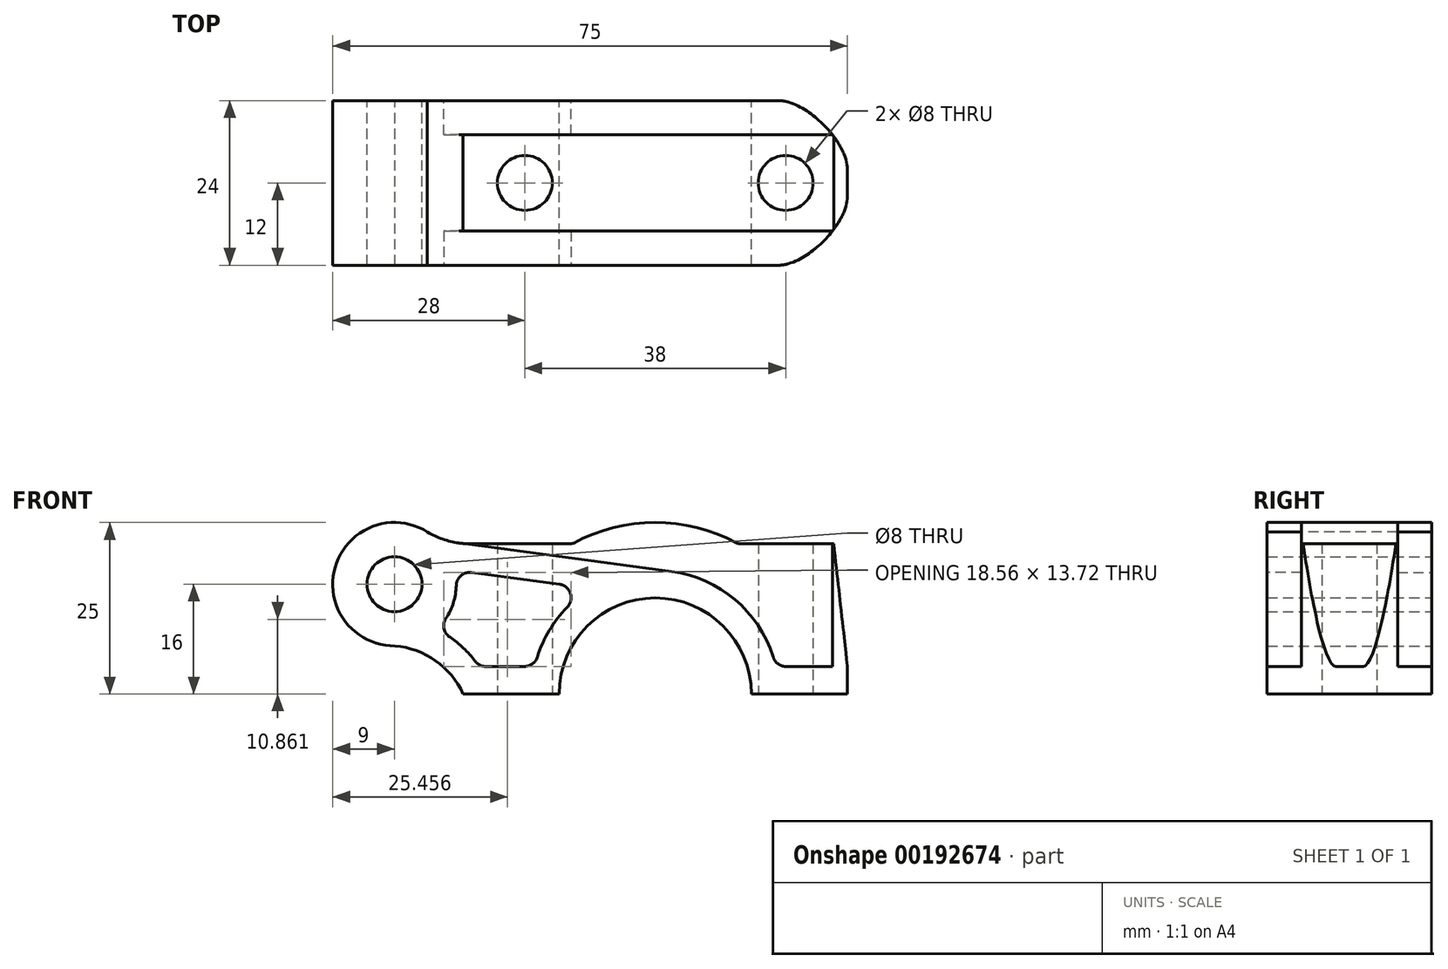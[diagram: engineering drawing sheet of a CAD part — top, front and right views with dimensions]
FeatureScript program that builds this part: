
annotation { "Feature Type Name" : "Feature", "Feature Type Description" : "" }
export const myFeature = defineFeature(function(context is Context, id is Id, definition is map)
    precondition{}
    {
        {
            var Q0;
            Q0=qCreatedBy(makeId("Front.planeOp"),FACE);
            var sketch = newSketch(context, id + "F0", { "sketchPlane" : qUnion([Q0])});
            skLineSegment(sketch, "E0.bottom", {"start": v(-28, 0) * mm, "end": v(-14, 0) * mm});
            skLineSegment(sketch, "E0.top", {"start": v(-28, 25) * mm, "end": v(28, 25) * mm});
            skLineSegment(sketch, "E0.left", {"start": v(-28, 0) * mm, "end": v(-28, 25) * mm});
            skLineSegment(sketch, "E0.right", {"start": v(28, 0) * mm, "end": v(28, 25) * mm});
            skArc(sketch, "E1", {"start": v(14, 0) * mm, "mid": v(0, 14) * mm, "end": v(-14, 0) * mm});
            skLineSegment(sketch, "E2.trimOffspring", {"start": v(14, 0) * mm, "end": v(28, 0) * mm});
            skSolve(sketch);
        }
        {
            var Q0;
            Q0 = qSketchRegion(id + "F0", true);
            extrude(context, id + "F1", {"entities" : qUnion([Q0]), "depth" : 24 * mm});
        }
        {
            var Q0;
            Q0=qCreatedBy(makeId("Top.planeOp"),FACE);
            var sketch = newSketch(context, id + "F2", { "sketchPlane" : qUnion([Q0])});
            skLineSegment(sketch, "E3", {"start": v(-28, -12) * mm, "end": v(28, -12) * mm, "construction": true});
            skCircle(sketch, "E4", {"center": v(-19, -12) * mm, "radius": 4 * mm});
            skCircle(sketch, "E5", {"center": v(19, -12) * mm, "radius": 4 * mm});
            skSolve(sketch);
        }
        {
            var Q0;
            Q0 = qSketchRegion(id + "F2", true);
            extrude(context, id + "F3", {"entities" : qUnion([Q0]), "operationType" : NewBodyOperationType.REMOVE, "endBound" : BoundingType.THROUGH_ALL, "depth" : 25 * mm});
        }
        {
            var Q0;
            Q0=qCreatedBy(makeId("Front.planeOp"),FACE);
            var sketch = newSketch(context, id + "F4", { "sketchPlane" : qUnion([Q0])});
            skCircle(sketch, "E6", {"center": v(-38, 16) * mm, "radius": 4 * mm});
            skArc(sketch, "E7", {"start": v(-38, 25) * mm, "mid": v(-47, 15.96) * mm, "end": v(-37.93, 7) * mm});
            skLineSegment(sketch, "E8", {"start": v(-38, 25) * mm, "end": v(-28, 25) * mm});
            skLineSegment(sketch, "E9", {"start": v(-28, 25) * mm, "end": v(-28, 0) * mm});
            skArc(sketch, "E10", {"start": v(-28, 0) * mm, "mid": v(-32.01, 4.85) * mm, "end": v(-37.93, 7) * mm});
            skSolve(sketch);
        }
        {
            var Q0;
            Q0 = qSketchRegion(id + "F4", true);
            extrude(context, id + "F5", {"entities" : qUnion([Q0]), "operationType" : NewBodyOperationType.ADD, "depth" : 24 * mm});
        }
        {
            var Q0;
            Q0=makeQuery(id+"F5.boolean.opBoolean","MERGE",FACE,{"derivedFrom":[makeQuery(id+"F1.opExtrude","CAP_FACE",FACE,{"disambiguationData":[OSD([sQuery(id+"F0.wireOp",EDGE,"E0.bottom"),sQuery(id+"F0.wireOp",EDGE,"E0.top"),sQuery(id+"F0.wireOp",EDGE,"E0.left"),sQuery(id+"F0.wireOp",EDGE,"E0.right"),sQuery(id+"F0.wireOp",EDGE,"E1"),sQuery(id+"F0.wireOp",EDGE,"E2.trimOffspring")])],"isStart":false}),makeQuery(id+"F5.opExtrude","CAP_FACE",FACE,{"disambiguationData":[OSD([sQuery(id+"F4.wireOp",EDGE,"E6"),sQuery(id+"F4.wireOp",EDGE,"E7"),sQuery(id+"F4.wireOp",EDGE,"E8"),sQuery(id+"F4.wireOp",EDGE,"E9"),sQuery(id+"F4.wireOp",EDGE,"E10")])],"isStart":false})]});
            var sketch = newSketch(context, id + "F6", { "sketchPlane" : qUnion([Q0])});
            skArc(sketch, "E11", {"start": v(12, 21.93) * mm, "mid": v(0, 25) * mm, "end": v(-12, 21.93) * mm});
            skLineSegment(sketch, "E12.bottom", {"start": v(12, 21.93) * mm, "end": v(28, 21.93) * mm});
            skLineSegment(sketch, "E12.top", {"start": v(12, 25) * mm, "end": v(28, 25) * mm});
            skLineSegment(sketch, "E12.right", {"start": v(28, 21.93) * mm, "end": v(28, 25) * mm});
            skLineSegment(sketch, "E13.MirrorCS", {"start": v(-12, 25) * mm, "end": v(-28, 25) * mm});
            skLineSegment(sketch, "E14.MirrorCS", {"start": v(-12, 21.93) * mm, "end": v(-28, 21.93) * mm});
            skLineSegment(sketch, "E15", {"start": v(12, 25) * mm, "end": v(-12, 25) * mm});
            skPoint(sketch, "E16.MirrorCS.start.orphan", {"position": v(-12, 21.93) * mm});
            skArc(sketch, "E17", {"start": v(-33.2, 23.61) * mm, "mid": v(-35.5, 24.65) * mm, "end": v(-38, 25) * mm});
            skLineSegment(sketch, "E18", {"start": v(-28, 25) * mm, "end": v(-38, 25) * mm});
            skPoint(sketch, "E19.MirrorCS.end.orphan", {"position": v(-28, 25) * mm});
            skPoint(sketch, "E20.start.orphan", {"position": v(-28, 21.93) * mm});
            skArc(sketch, "E21", {"start": v(-33.2, 23.61) * mm, "mid": v(-30.7, 22.47) * mm, "end": v(-28, 21.93) * mm});
            skSolve(sketch);
        }
        {
            var Q0;
            Q0 = qSketchRegion(id + "F6", true);
            extrude(context, id + "F7", {"entities" : qUnion([Q0]), "operationType" : NewBodyOperationType.REMOVE, "endBound" : BoundingType.THROUGH_ALL, "oppositeDirection" : true, "depth" : 25 * mm});
        }
        {
            var Q0;
            Q0=makeQuery(id+"F5.boolean.opBoolean","MERGE",FACE,{"derivedFrom":[makeQuery(id+"F1.opExtrude","CAP_FACE",FACE,{"disambiguationData":[OSD([sQuery(id+"F0.wireOp",EDGE,"E0.bottom"),sQuery(id+"F0.wireOp",EDGE,"E0.top"),sQuery(id+"F0.wireOp",EDGE,"E0.left"),sQuery(id+"F0.wireOp",EDGE,"E0.right"),sQuery(id+"F0.wireOp",EDGE,"E1"),sQuery(id+"F0.wireOp",EDGE,"E2.trimOffspring")])],"isStart":false}),makeQuery(id+"F5.opExtrude","CAP_FACE",FACE,{"disambiguationData":[OSD([sQuery(id+"F4.wireOp",EDGE,"E6"),sQuery(id+"F4.wireOp",EDGE,"E7"),sQuery(id+"F4.wireOp",EDGE,"E8"),sQuery(id+"F4.wireOp",EDGE,"E9"),sQuery(id+"F4.wireOp",EDGE,"E10")])],"isStart":false})]});
            var sketch = newSketch(context, id + "F8", { "sketchPlane" : qUnion([Q0])});
            skArc(sketch, "E22", {"start": v(17.55, 4) * mm, "mid": v(12.14, 13.3) * mm, "end": v(2.4, 17.84) * mm});
            skLineSegment(sketch, "E23", {"start": v(17.55, 4) * mm, "end": v(28, 4) * mm});
            skLineSegment(sketch, "E24", {"start": v(-17.55, 4) * mm, "end": v(-25.67, 4) * mm});
            skArc(sketch, "E25", {"start": v(-25.67, 4) * mm, "mid": v(-27.6, 6.34) * mm, "end": v(-29.94, 8.28) * mm});
            skArc(sketch, "E26", {"start": v(-30.5, 11.04) * mm, "mid": v(-29.41, 13.3) * mm, "end": v(-29, 15.78) * mm});
            skArc(sketch, "E27", {"start": v(-30.5, 11.04) * mm, "mid": v(-30.78, 9.55) * mm, "end": v(-29.94, 8.28) * mm});
            skLineSegment(sketch, "E28", {"start": v(28, 4) * mm, "end": v(28, 25) * mm});
            skLineSegment(sketch, "E29", {"start": v(-38, 25) * mm, "end": v(28, 25) * mm});
            skArc(sketch, "E30", {"start": v(-33.2, 23.61) * mm, "mid": v(-30.98, 22.57) * mm, "end": v(-28.6, 22) * mm});
            skLineSegment(sketch, "E31", {"start": v(-28.6, 22) * mm, "end": v(2.4, 17.84) * mm});
            skLineSegment(sketch, "E32", {"start": v(-26.74, 17.71) * mm, "end": v(-14, 16) * mm});
            skArc(sketch, "E33", {"start": v(-26.74, 17.71) * mm, "mid": v(-28.3, 17.25) * mm, "end": v(-29, 15.78) * mm});
            skArc(sketch, "E34", {"start": v(-12.84, 12.62) * mm, "mid": v(-12.37, 14.67) * mm, "end": v(-14, 16) * mm});
            skArc(sketch, "E35.trimOffspring", {"start": v(-12.84, 12.62) * mm, "mid": v(-15.8, 8.64) * mm, "end": v(-17.55, 4) * mm});
            skArc(sketch, "E36.trimOffspring", {"start": v(-33.2, 23.61) * mm, "mid": v(-35.5, 24.65) * mm, "end": v(-38, 25) * mm});
            skSolve(sketch);
        }
        {
            var Q0;
            Q0 = qSketchRegion(id + "F8", true);
            extrude(context, id + "F9", {"entities" : qUnion([Q0]), "operationType" : NewBodyOperationType.REMOVE, "oppositeDirection" : true, "depth" : 5 * mm});
        }
        {
            var Q0;
            Q0=qCreatedBy(makeId("Front.planeOp"),FACE);
            cPlane(context, id + "F10", {"entities" : qUnion([Q0]), "cplaneType" : CPlaneType.OFFSET, "offset" : 12 * mm, "width" : 150 * mm, "height" : 150 * mm});
        }
        {
            var Q0;
            Q0=qCreatedBy(id+"F10.planeOp",FACE);
            var sketch = newSketch(context, id + "F11", { "sketchPlane" : qUnion([Q0])});
            skLineSegment(sketch, "E37.bottom", {"start": v(36.92, 42.36) * mm, "end": v(-64.03, 42.36) * mm});
            skLineSegment(sketch, "E37.top", {"start": v(36.92, -24.17) * mm, "end": v(-64.03, -24.17) * mm});
            skLineSegment(sketch, "E37.left", {"start": v(36.92, 42.36) * mm, "end": v(36.92, -24.17) * mm});
            skLineSegment(sketch, "E37.right", {"start": v(-64.03, 42.36) * mm, "end": v(-64.03, -24.17) * mm});
            skSolve(sketch);
        }
        {
            var Q0;
            Q0 = qSketchRegion(id + "F11", true);
            extrude(context, id + "F12", {"entities" : qUnion([Q0]), "operationType" : NewBodyOperationType.REMOVE, "endBound" : BoundingType.THROUGH_ALL, "oppositeDirection" : true, "depth" : 25 * mm});
        }
        {
            var Q0;
            Q0=makeQuery(id+"F9.boolean.opBoolean","COPY",FACE,{"derivedFrom":makeQuery(id+"F9.opExtrude","CAP_FACE",FACE,{"disambiguationData":[OSD([sQuery(id+"F8.wireOp",EDGE,"E22"),sQuery(id+"F8.wireOp",EDGE,"E23"),sQuery(id+"F8.wireOp",EDGE,"E24"),sQuery(id+"F8.wireOp",EDGE,"E25"),sQuery(id+"F8.wireOp",EDGE,"E26"),sQuery(id+"F8.wireOp",EDGE,"E27"),sQuery(id+"F8.wireOp",EDGE,"E28"),sQuery(id+"F8.wireOp",EDGE,"E29")])],"isStart":false})});
            var sketch = newSketch(context, id + "F13", { "sketchPlane" : qUnion([Q0])});
            skLineSegment(sketch, "E38", {"start": v(28, 4) * mm, "end": v(28, 21.93) * mm});
            skLineSegment(sketch, "E39", {"start": v(28, 21.93) * mm, "end": v(26, 21.93) * mm});
            skLineSegment(sketch, "E40", {"start": v(26, 21.93) * mm, "end": v(28, 4) * mm});
            skSolve(sketch);
        }
        {
            var Q0;
            Q0 = qSketchRegion(id + "F13", true);
            extrude(context, id + "F14", {"entities" : qUnion([Q0]), "operationType" : NewBodyOperationType.REMOVE, "endBound" : BoundingType.THROUGH_ALL, "oppositeDirection" : true, "depth" : 25 * mm});
        }
        {
            var Q0;
            Q0=makeQuery(id+"F9.boolean.opBoolean","COPY",EDGE,{"derivedFrom":makeQuery(id+"F9.opExtrude","SWEPT_EDGE",EDGE,{"disambiguationData":[OSD([sQuery(id+"F8.wireOp",EDGE,"E24"),sQuery(id+"F8.wireOp",EDGE,"E25")])]})});
            var Q1;
            Q1=makeQuery(id+"F9.boolean.opBoolean","COPY",EDGE,{"derivedFrom":makeQuery(id+"F9.opExtrude","SWEPT_EDGE",EDGE,{"disambiguationData":[OSD([sQuery(id+"F8.wireOp",EDGE,"E24"),sQuery(id+"F8.wireOp",EDGE,"E35.trimOffspring")])]})});
            var Q2;
            Q2=makeQuery(id+"F9.boolean.opBoolean","COPY",EDGE,{"derivedFrom":makeQuery(id+"F9.opExtrude","SWEPT_EDGE",EDGE,{"disambiguationData":[OSD([sQuery(id+"F8.wireOp",EDGE,"E22"),sQuery(id+"F8.wireOp",EDGE,"E23")])]})});
            fillet(context, id + "F15", {"entities" : qUnion([Q0, Q1, Q2]), "radius" : 2 * mm, "tangentPropagation" : true, "allowEdgeOverflow" : false});
        }
        {
            var Q0;
            Q0=makeQuery(id+"F1.opExtrude","SWEPT_BODY",BODY,{"disambiguationData":[OSD([sQuery(id+"F0.wireOp",EDGE,"E0.bottom"),sQuery(id+"F0.wireOp",EDGE,"E0.top"),sQuery(id+"F0.wireOp",EDGE,"E0.left"),sQuery(id+"F0.wireOp",EDGE,"E0.right"),sQuery(id+"F0.wireOp",EDGE,"E1"),sQuery(id+"F0.wireOp",EDGE,"E2.trimOffspring")])]});
            var Q1;
            Q1=qCreatedBy(id+"F10.planeOp",FACE);
            mirror(context, id + "F16", {"operationType" : NewBodyOperationType.ADD, "entities" : qUnion([Q0]), "mirrorPlane" : qUnion([Q1])});
        }
        {
            var Q0;
            {var subQ0=makeQuery(id+"F14.boolean.opBoolean","COPY",EDGE,{"derivedFrom":makeQuery(id+"F14.opExtrude","SWEPT_EDGE",EDGE,{"disambiguationData":[OSD([sQuery(id+"F6.wireOp",EDGE,"E12.bottom"),sQuery(id+"F8.wireOp",EDGE,"E22"),sQuery(id+"F8.wireOp",EDGE,"E23"),sQuery(id+"F8.wireOp",EDGE,"E28"),sQuery(id+"F8.wireOp",EDGE,"E29"),sQuery(id+"F8.wireOp",EDGE,"E30"),sQuery(id+"F8.wireOp",EDGE,"E31"),sQuery(id+"F8.wireOp",EDGE,"E36.trimOffspring"),sQuery(id+"F13.wireOp",EDGE,"E39"),sQuery(id+"F13.wireOp",EDGE,"E40")])]})});Q0=makeQuery(id+"F16.boolean.opBoolean","MERGE",EDGE,{"derivedFrom":[subQ0,makeQuery(id+"F16.opPattern","COPY",EDGE,{"derivedFrom":subQ0,"instanceName":"1"})]});}
            var Q1;
            {var subQ0=makeQuery(id+"F7.boolean.opBoolean","COPY",EDGE,{"derivedFrom":makeQuery(id+"F7.opExtrude","SWEPT_EDGE",EDGE,{"disambiguationData":[OSD([sQuery(id+"F6.wireOp",EDGE,"E11"),sQuery(id+"F6.wireOp",EDGE,"E12.bottom")])]})});Q1=makeQuery(id+"F16.boolean.opBoolean","MERGE",EDGE,{"derivedFrom":[subQ0,makeQuery(id+"F16.opPattern","COPY",EDGE,{"derivedFrom":subQ0,"instanceName":"1"})]});}
            var Q2;
            {var subQ0=makeQuery(id+"F7.boolean.opBoolean","COPY",EDGE,{"derivedFrom":makeQuery(id+"F7.opExtrude","SWEPT_EDGE",EDGE,{"disambiguationData":[OSD([sQuery(id+"F6.wireOp",EDGE,"E11"),sQuery(id+"F6.wireOp",EDGE,"E14.MirrorCS")])]})});Q2=makeQuery(id+"F16.boolean.opBoolean","MERGE",EDGE,{"derivedFrom":[subQ0,makeQuery(id+"F16.opPattern","COPY",EDGE,{"derivedFrom":subQ0,"instanceName":"1"})]});}
            fillet(context, id + "F17", {"entities" : qUnion([Q0, Q1, Q2]), "radius" : .5 * mm, "tangentPropagation" : true, "allowEdgeOverflow" : false});
        }
        {
            var Q0;
            Q0=makeQuery(id+"F1.opExtrude","CAP_EDGE",EDGE,{"disambiguationData":[OSD([sQuery(id+"F0.wireOp",EDGE,"E0.right")])],"isStart":false});
            var Q1;
            Q1=makeQuery(id+"F16.opPattern","COPY",EDGE,{"derivedFrom":makeQuery(id+"F1.opExtrude","CAP_EDGE",EDGE,{"disambiguationData":[OSD([sQuery(id+"F0.wireOp",EDGE,"E0.right")])],"isStart":false}),"instanceName":"1"});
            fillet(context, id + "F18", {"entities" : qUnion([Q0, Q1]), "radius" : 10 * mm, "tangentPropagation" : true, "rho" : .3, "crossSection" : FilletCrossSection.CONIC, "allowEdgeOverflow" : false});
        }
    });
